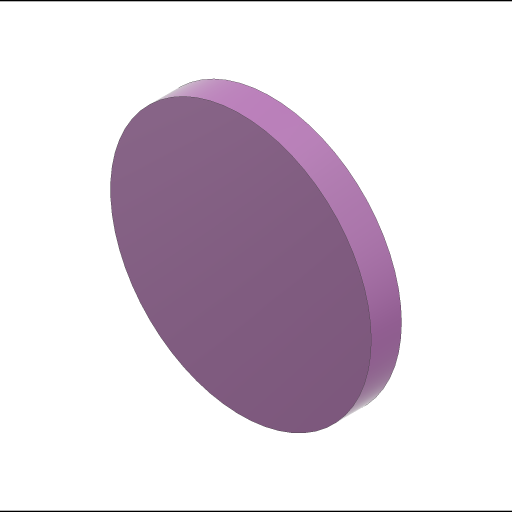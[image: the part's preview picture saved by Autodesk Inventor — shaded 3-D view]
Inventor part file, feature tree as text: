
AUTODESK INVENTOR PART (.ipt)
format: ipt  version: 2023 (Build 270158000, 158)  size: 96,256 bytes
history: native  units: in
note: dims shown in document units (in); Inventor stores cm internally (conversion verified against a paired STEP export)
features: extrude x1, sketch x1
ambient origin geometry x8: Origin, YZ Plane, XZ Plane, XY Plane, X Axis, Y Axis, Z Axis, Center Point
bodies: Solid1 (feature_tree)
feature tree (2):
  extrude  "Extrusion1"  Depth=2.0in TaperAngle=0.0deg
  sketch  "Sketch1"  dims[d0=17.2441in d1=2.0in d2=0.0in]
